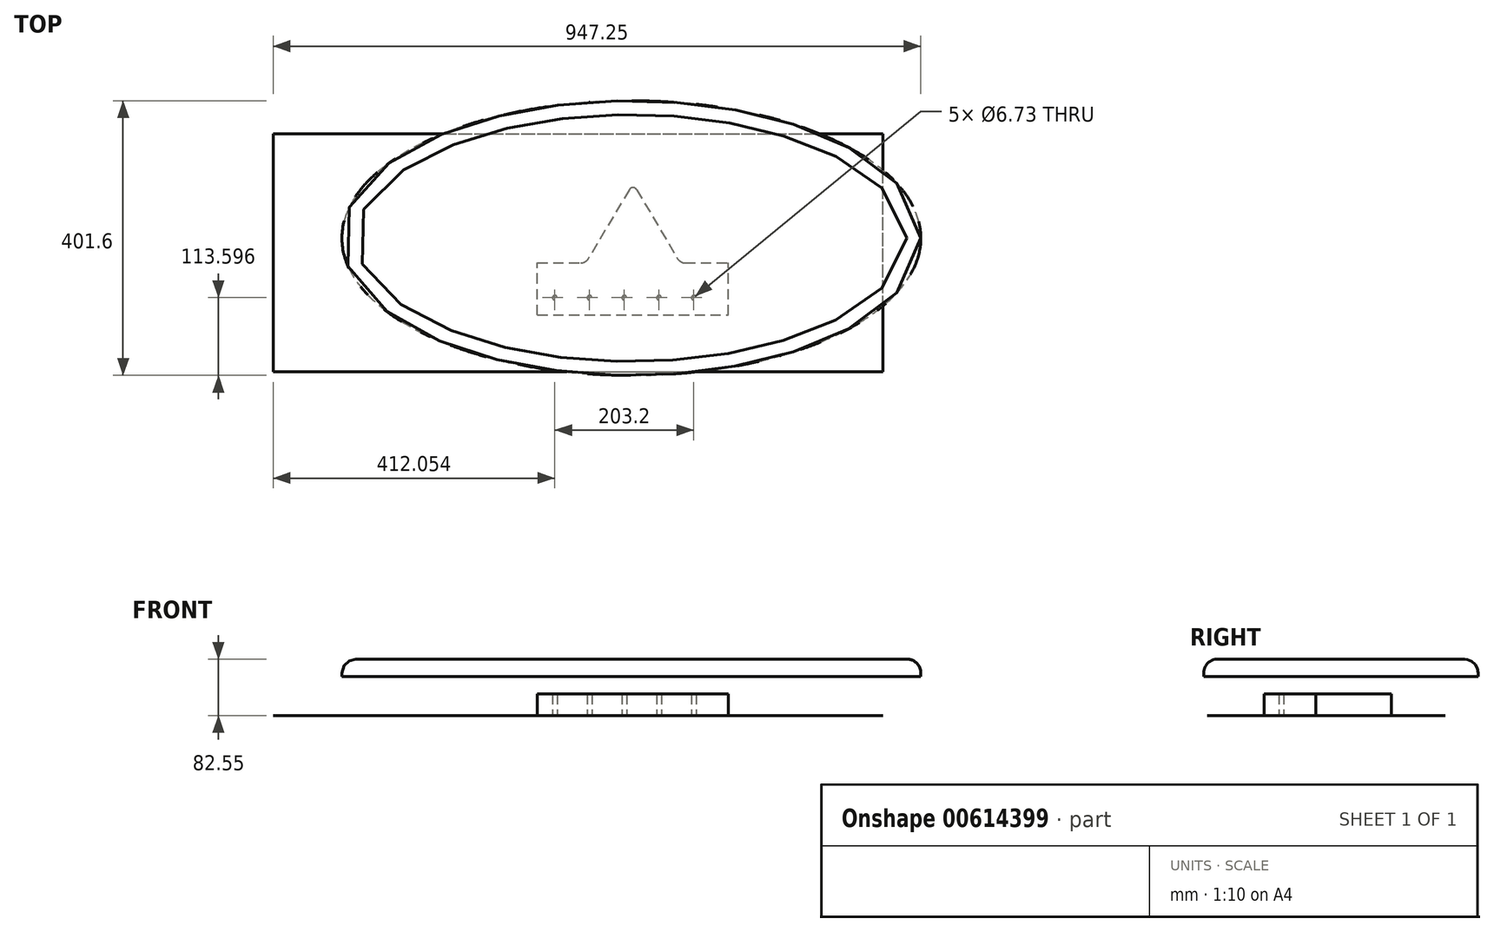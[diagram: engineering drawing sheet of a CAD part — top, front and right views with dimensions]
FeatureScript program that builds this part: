
annotation { "Feature Type Name" : "Feature", "Feature Type Description" : "" }
export const myFeature = defineFeature(function(context is Context, id is Id, definition is map)
    precondition{}
    {
        {
            var Q0;
            Q0=qCreatedBy(makeId("Top.planeOp"),FACE);
            var sketch = newSketch(context, id + "F0", { "sketchPlane" : qUnion([Q0])});
            skLineSegment(sketch, "E0.bottom", {"start": v(406.54, 83.1) * mm, "end": v(685.94, 83.1) * mm});
            skLineSegment(sketch, "E0.top", {"start": v(406.54, 159.3) * mm, "end": v(469.93, 159.3) * mm});
            skLineSegment(sketch, "E0.left", {"start": v(406.54, 83.1) * mm, "end": v(406.54, 159.3) * mm});
            skLineSegment(sketch, "E0.right", {"start": v(685.94, 83.1) * mm, "end": v(685.94, 159.3) * mm});
            skLineSegment(sketch, "E1", {"start": v(546.24, 275.6) * mm, "end": v(546.24, 63.17) * mm, "construction": true});
            skPoint(sketch, "E1.startSnap0", {"position": v(546.24, 159.3) * mm});
            skLineSegment(sketch, "E2", {"start": v(540.78, 266.41) * mm, "end": v(480.85, 165.52) * mm});
            skLineSegment(sketch, "E3.MirrorCS", {"start": v(551.7, 266.41) * mm, "end": v(611.64, 165.52) * mm});
            skPoint(sketch, "E4.visualSharp", {"position": v(546.24, 275.6) * mm});
            skArc(sketch, "E4.filletArc", {"start": v(551.7, 266.41) * mm, "mid": v(546.24, 269.52) * mm, "end": v(540.78, 266.41) * mm});
            skLineSegment(sketch, "E5.trimOffspring", {"start": v(622.56, 159.3) * mm, "end": v(685.94, 159.3) * mm});
            skPoint(sketch, "E6.visualSharp", {"position": v(477.15, 159.3) * mm});
            skArc(sketch, "E6.filletArc", {"start": v(469.93, 159.3) * mm, "mid": v(476.2, 160.97) * mm, "end": v(480.85, 165.52) * mm});
            skPoint(sketch, "E7.visualSharp", {"position": v(615.33, 159.3) * mm});
            skArc(sketch, "E7.filletArc", {"start": v(611.64, 165.52) * mm, "mid": v(616.28, 160.97) * mm, "end": v(622.56, 159.3) * mm});
            skCircle(sketch, "E8", {"center": v(431.94, 108.5) * mm, "radius": 3.37 * mm});
            skCircle(sketch, "E9.1.0.0", {"center": v(482.74, 108.5) * mm, "radius": 3.37 * mm});
            skCircle(sketch, "E9.2.0.0", {"center": v(533.54, 108.5) * mm, "radius": 3.37 * mm});
            skCircle(sketch, "E9.3.0.0", {"center": v(584.34, 108.5) * mm, "radius": 3.37 * mm});
            skCircle(sketch, "E9.4.0.0", {"center": v(635.14, 108.5) * mm, "radius": 3.37 * mm});
            skLineSegment(sketch, "E9.direction1", {"start": v(431.94, 108.5) * mm, "end": v(482.74, 108.5) * mm, "construction": true});
            skSolve(sketch);
        }
        {
            var Q0;
            Q0 = qSketchRegion(id + "F0", true);
            extrude(context, id + "F1", {"entities" : qUnion([Q0]), "depth" : 31.75 * mm, "offsetDistance" : 25.4 * mm});
        }
        {
            var Q0;
            Q0=qCreatedBy(makeId("Top.planeOp"),FACE);
            var sketch = newSketch(context, id + "F2", { "sketchPlane" : qUnion([Q0])});
            skLineSegment(sketch, "E10.bottom", {"start": v(19.9, 0) * mm, "end": v(911.57, 0) * mm});
            skLineSegment(sketch, "E10.top", {"start": v(19.9, 348.03) * mm, "end": v(911.57, 348.03) * mm});
            skLineSegment(sketch, "E10.left", {"start": v(19.9, 0) * mm, "end": v(19.9, 348.03) * mm});
            skLineSegment(sketch, "E10.right", {"start": v(911.57, 0) * mm, "end": v(911.57, 348.03) * mm});
            skSolve(sketch);
        }
        {
            var Q0;
            Q0 = qSketchRegion(id + "F2", true);
            extrude(context, id + "F3", {"entities" : qUnion([Q0]), "depth" : 0.03 * mm, "offsetDistance" : 25.4 * mm});
        }
        {
            var Q0;
            Q0=qCreatedBy(makeId("Top.planeOp"),FACE);
            cPlane(context, id + "F4", {"entities" : qUnion([Q0]), "cplaneType" : CPlaneType.OFFSET, "offset" : 57.15 * mm, "width" : 152.4 * mm, "height" : 152.4 * mm});
        }
        {
            var Q0;
            Q0=qCreatedBy(id+"F4.planeOp",FACE);
            var sketch = newSketch(context, id + "F5", { "sketchPlane" : qUnion([Q0])});
            skEllipse(sketch, "E11", {"center": v(543.84, 195.71) * mm, "majorRadius": 423.3 * mm, "minorRadius": 200.8 * mm, "majorAxis": v(1, 0)});
            skSolve(sketch);
        }
        {
            var Q0;
            Q0 = qSketchRegion(id + "F5", true);
            extrude(context, id + "F6", {"entities" : qUnion([Q0]), "depth" : 25.4 * mm, "offsetDistance" : 25.4 * mm});
        }
        {
            var Q0;
            Q0=makeQuery(id+"F6.opExtrude","CAP_EDGE",EDGE,{"disambiguationData":[OSD([sQuery(id+"F5.wireOp",EDGE,"E11")])],"isStart":false});
            fillet(context, id + "F7", {"entities" : qUnion([Q0]), "radius" : 20.32 * mm, "tangentPropagation" : true, "allowEdgeOverflow" : false});
        }
    });
